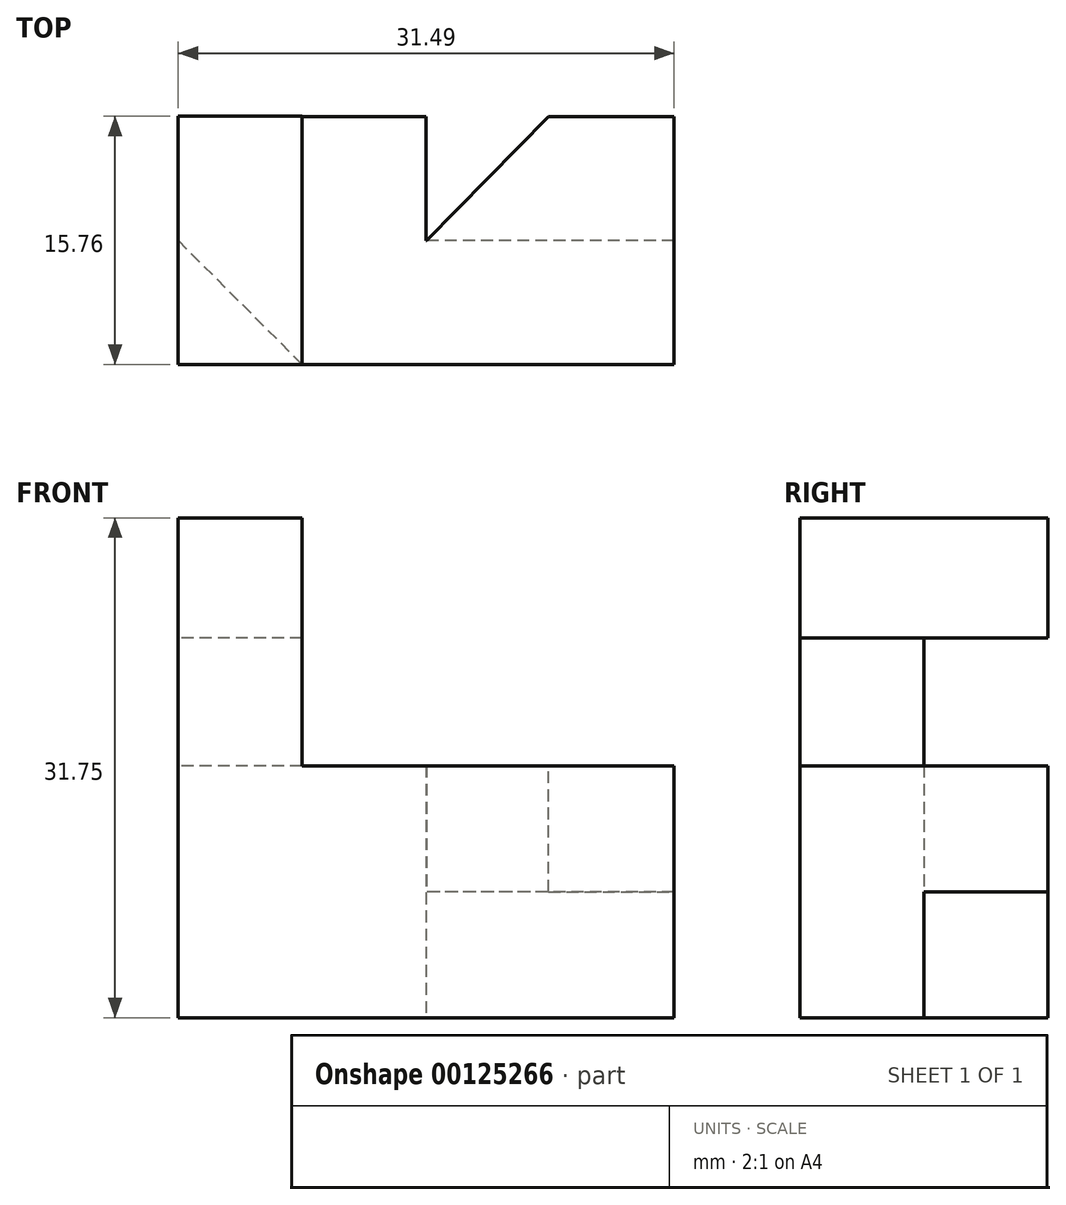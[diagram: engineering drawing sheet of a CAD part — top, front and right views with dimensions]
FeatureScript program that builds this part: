
annotation { "Feature Type Name" : "Feature", "Feature Type Description" : "" }
export const myFeature = defineFeature(function(context is Context, id is Id, definition is map)
    precondition{}
    {
        {
            var Q0;
            Q0=qCreatedBy(makeId("Top.planeOp"),FACE);
            var sketch = newSketch(context, id + "F0", { "sketchPlane" : qUnion([Q0])});
            skLineSegment(sketch, "E0.bottom", {"start": v(7.87, 7.87) * mm, "end": v(-7.87, 7.87) * mm});
            skLineSegment(sketch, "E0.top", {"start": v(7.87, -7.87) * mm, "end": v(-7.87, -7.87) * mm});
            skLineSegment(sketch, "E0.left", {"start": v(7.87, 7.87) * mm, "end": v(7.87, -7.87) * mm});
            skLineSegment(sketch, "E0.right", {"start": v(-7.87, 7.87) * mm, "end": v(-7.87, -7.87) * mm});
            skPoint(sketch, "E0.middle", {"position": v(0, 0) * mm});
            skSolve(sketch);
        }
        {
            var Q0;
            Q0 = qSketchRegion(id + "F0", true);
            extrude(context, id + "F1", {"entities" : qUnion([Q0]), "depth" : 16 * mm});
        }
        {
            var Q0;
            Q0=makeQuery(id+"F1.opExtrude","CAP_FACE",FACE,{"disambiguationData":[OSD([sQuery(id+"F0.wireOp",EDGE,"E0.bottom"),sQuery(id+"F0.wireOp",EDGE,"E0.top"),sQuery(id+"F0.wireOp",EDGE,"E0.left"),sQuery(id+"F0.wireOp",EDGE,"E0.right")])],"isStart":false});
            var sketch = newSketch(context, id + "F2", { "sketchPlane" : qUnion([Q0])});
            skLineSegment(sketch, "E1", {"start": v(-7.87, 0) * mm, "end": v(-7.87, -7.87) * mm});
            skLineSegment(sketch, "E2", {"start": v(-7.87, -7.87) * mm, "end": v(0, -7.87) * mm});
            skLineSegment(sketch, "E3", {"start": v(0, -7.87) * mm, "end": v(-7.87, 0) * mm});
            skSolve(sketch);
        }
        {
            var Q0;
            Q0=makeQuery(id+"F2.imprint","IMPRINT",FACE,{"disambiguationData":[TD([[makeQuery(id+"F2.imprint","IMPRINT",EDGE,{"derivedFrom":sQuery(id+"F2.wireOp",EDGE,"E1")}),1.0]])]});
            extrude(context, id + "F3", {"entities" : qUnion([Q0]), "operationType" : NewBodyOperationType.ADD, "depth" : 8.13 * mm});
        }
        {
            var Q0;
            Q0=makeQuery(id+"F3.opExtrude","CAP_FACE",FACE,{"disambiguationData":[OSD([sQuery(id+"F2.wireOp",EDGE,"E1"),sQuery(id+"F2.wireOp",EDGE,"E2"),sQuery(id+"F2.wireOp",EDGE,"E3")])],"isStart":false});
            var sketch = newSketch(context, id + "F4", { "sketchPlane" : qUnion([Q0])});
            skLineSegment(sketch, "E4.bottom", {"start": v(-7.87, -7.87) * mm, "end": v(0, -7.87) * mm});
            skLineSegment(sketch, "E4.top", {"start": v(-7.87, 7.89) * mm, "end": v(0, 7.89) * mm});
            skLineSegment(sketch, "E4.left", {"start": v(-7.87, -7.87) * mm, "end": v(-7.87, 7.89) * mm});
            skLineSegment(sketch, "E4.right", {"start": v(0, -7.87) * mm, "end": v(0, 7.89) * mm});
            skSolve(sketch);
        }
        {
            var Q0;
            {var subQ0=sQuery(id+"F4.wireOp",EDGE,"E4.top");Q0=makeQuery(id+"F4.imprint","IMPRINT",FACE,{"disambiguationData":[TD([[makeQuery(id+"F4.imprint","IMPRINT",EDGE,{"derivedFrom":subQ0}),-1.0]])]});}
            var Q1;
            {var subQ0=sQuery(id+"F4.wireOp",EDGE,"E4.bottom");Q1=makeQuery(id+"F4.imprint","IMPRINT",FACE,{"disambiguationData":[TD([[makeQuery(id+"F4.imprint","IMPRINT",EDGE,{"derivedFrom":subQ0}),-1.0]])]});}
            extrude(context, id + "F5", {"entities" : qUnion([Q0, Q1]), "operationType" : NewBodyOperationType.ADD, "depth" : 7.62 * mm});
        }
        {
            var Q0;
            Q0=makeQuery(id+"F1.opExtrude","SWEPT_FACE",FACE,{"disambiguationData":[OSD([sQuery(id+"F0.wireOp",EDGE,"E0.left")])]});
            var sketch = newSketch(context, id + "F6", { "sketchPlane" : qUnion([Q0])});
            skLineSegment(sketch, "E5.bottom", {"start": v(-7.87, 16) * mm, "end": v(0, 16) * mm});
            skLineSegment(sketch, "E5.top", {"start": v(-7.87, 0) * mm, "end": v(0, 0) * mm});
            skLineSegment(sketch, "E5.left", {"start": v(-7.87, 16) * mm, "end": v(-7.87, 0) * mm});
            skLineSegment(sketch, "E5.right", {"start": v(0, 16) * mm, "end": v(0, 0) * mm});
            skSolve(sketch);
        }
        {
            var Q0;
            Q0 = qSketchRegion(id + "F6", true);
            extrude(context, id + "F7", {"entities" : qUnion([Q0]), "operationType" : NewBodyOperationType.ADD, "depth" : 15.75 * mm});
        }
        {
            var Q0;
            Q0=makeQuery(id+"F7.opExtrude","SWEPT_FACE",FACE,{"disambiguationData":[OSD([sQuery(id+"F6.wireOp",EDGE,"E5.right")])]});
            var sketch = newSketch(context, id + "F8", { "sketchPlane" : qUnion([Q0])});
            skPoint(sketch, "E6.oppositeSnap0", {"position": v(-23.62, 8) * mm});
            skLineSegment(sketch, "E6.bottom", {"start": v(-23.62, 16) * mm, "end": v(-15.65, 16) * mm});
            skLineSegment(sketch, "E6.top", {"start": v(-23.62, 8) * mm, "end": v(-15.65, 8) * mm});
            skLineSegment(sketch, "E6.left", {"start": v(-23.62, 16) * mm, "end": v(-23.62, 8) * mm});
            skLineSegment(sketch, "E6.right", {"start": v(-15.65, 16) * mm, "end": v(-15.65, 8) * mm});
            skSolve(sketch);
        }
        {
            var Q0;
            Q0=makeQuery(id+"F8.imprint","IMPRINT",FACE,{"disambiguationData":[TD([[makeQuery(id+"F8.imprint","IMPRINT",EDGE,{"derivedFrom":sQuery(id+"F8.wireOp",EDGE,"E6.bottom")}),-1.0]])]});
            var Q1;
            Q1=makeQuery(id+"F1.opExtrude","SWEPT_FACE",FACE,{"disambiguationData":[OSD([sQuery(id+"F0.wireOp",EDGE,"E0.bottom")])]});
            extrude(context, id + "F9", {"entities" : qUnion([Q0]), "operationType" : NewBodyOperationType.ADD, "endBound" : BoundingType.UP_TO_SURFACE, "endBoundEntityFace" : qUnion([Q1]), "depth" : 25.4 * mm});
        }
        {
            var Q0;
            Q0=makeQuery(id+"F9.opExtrude","SWEPT_FACE",FACE,{"disambiguationData":[OSD([sQuery(id+"F8.wireOp",EDGE,"E6.top")])]});
            var sketch = newSketch(context, id + "F10", { "sketchPlane" : qUnion([Q0])});
            skLineSegment(sketch, "E7", {"start": v(15.65, -7.87) * mm, "end": v(7.87, 0.03) * mm});
            skLineSegment(sketch, "E8", {"start": v(7.87, 0.03) * mm, "end": v(15.65, 0) * mm});
            skSolve(sketch);
        }
        {
            var Q0;
            Q0 = qSketchRegion(id + "F10", true);
            var Q1;
            Q1=makeQuery(id+"F10.imprint","IMPRINT",FACE,{"disambiguationData":[TD([[makeQuery(id+"F10.imprint","IMPRINT",EDGE,{"derivedFrom":sQuery(id+"F10.wireOp",EDGE,"E7")}),-1.0]])]});
            var Q2;
            Q2=makeQuery(id+"F9.boolean.opBoolean","MERGE",FACE,{"derivedFrom":[makeQuery(id+"F7.boolean.opBoolean","MERGE",FACE,{"derivedFrom":[makeQuery(id+"F1.opExtrude","CAP_FACE",FACE,{"disambiguationData":[OSD([sQuery(id+"F0.wireOp",EDGE,"E0.bottom"),sQuery(id+"F0.wireOp",EDGE,"E0.top"),sQuery(id+"F0.wireOp",EDGE,"E0.left"),sQuery(id+"F0.wireOp",EDGE,"E0.right")])],"isStart":false}),makeQuery(id+"F7.opExtrude","SWEPT_FACE",FACE,{"disambiguationData":[OSD([sQuery(id+"F6.wireOp",EDGE,"E5.bottom")])]})]}),makeQuery(id+"F9.opExtrude","SWEPT_FACE",FACE,{"disambiguationData":[OSD([sQuery(id+"F8.wireOp",EDGE,"E6.bottom")])]})]});
            extrude(context, id + "F11", {"entities" : qUnion([Q0, Q1]), "operationType" : NewBodyOperationType.ADD, "endBound" : BoundingType.UP_TO_SURFACE, "oppositeDirection" : true, "endBoundEntityFace" : qUnion([Q2]), "depth" : 25.4 * mm});
        }
    });
